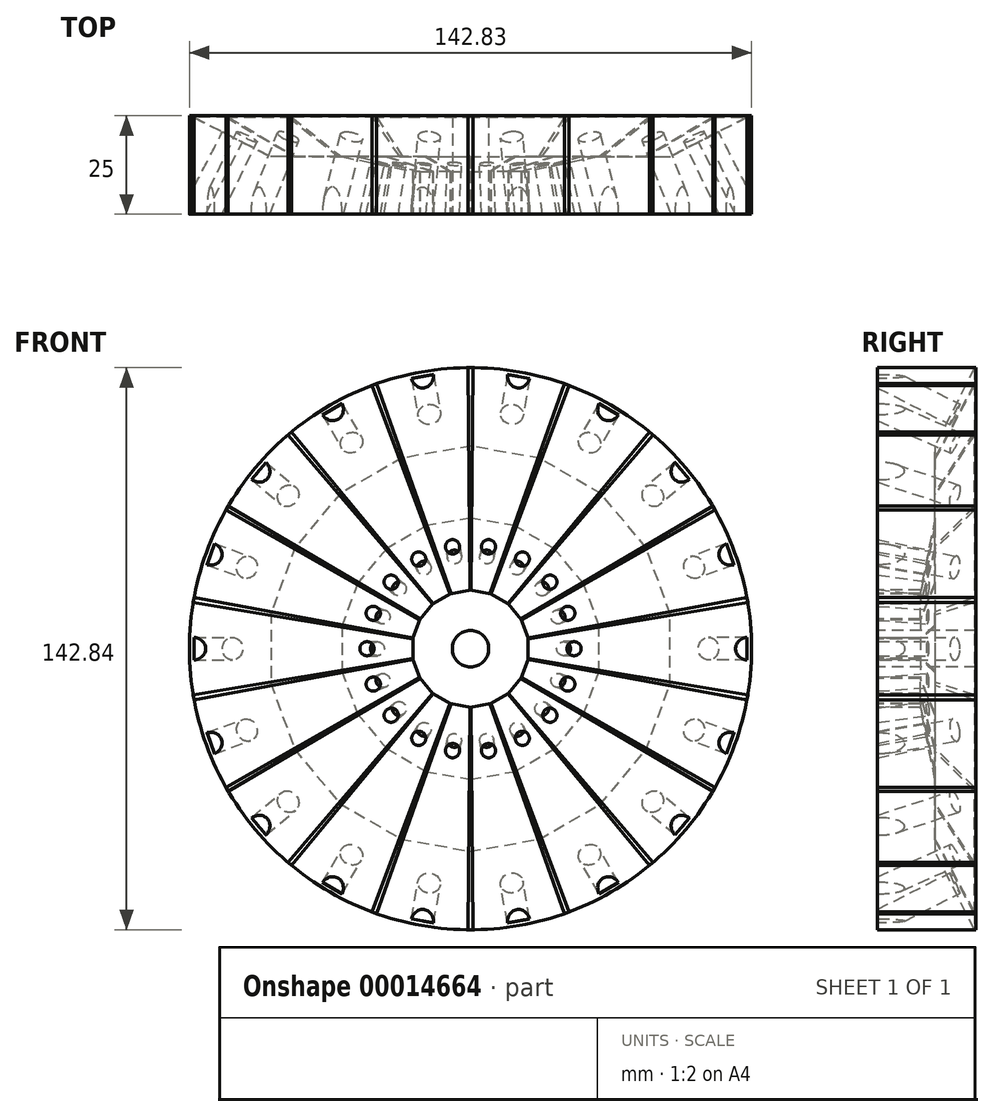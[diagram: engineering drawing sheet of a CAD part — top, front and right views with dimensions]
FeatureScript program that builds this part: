
annotation { "Feature Type Name" : "Feature", "Feature Type Description" : "" }
export const myFeature = defineFeature(function(context is Context, id is Id, definition is map)
    precondition{}
    {
        {
            var Q0;
            Q0=qCreatedBy(makeId("Top.planeOp"),FACE);
            var sketch = newSketch(context, id + "F0", { "sketchPlane" : qUnion([Q0])});
            skLineSegment(sketch, "E0.bottom", {"start": v(0, 0) * mm, "end": v(-36.04, 0) * mm});
            skLineSegment(sketch, "E0.top", {"start": v(-18.02, 14.6) * mm, "end": v(-36.04, 14.6) * mm});
            skLineSegment(sketch, "E0.left", {"start": v(0, 0) * mm, "end": v(0, 10.86) * mm});
            skLineSegment(sketch, "E0.right", {"start": v(-36.04, 0) * mm, "end": v(-36.04, 14.6) * mm});
            skLineSegment(sketch, "E1.bottom", {"start": v(-36.04, 0) * mm, "end": v(-55.59, 0) * mm});
            skLineSegment(sketch, "E1.right", {"start": v(-55.59, 0) * mm, "end": v(-55.59, 24.64) * mm});
            skLineSegment(sketch, "E2", {"start": v(-55.59, 24.64) * mm, "end": v(-36.04, 14.6) * mm});
            skLineSegment(sketch, "E3", {"start": v(-18.02, 14.6) * mm, "end": v(-18.02, 0) * mm});
            skLineSegment(sketch, "E4", {"start": v(-18.02, 14.6) * mm, "end": v(0, 10.86) * mm});
            skPoint(sketch, "E5.orphan", {"position": v(0, 14.6) * mm});
            skSolve(sketch);
        }
        {
            var Q0;
            {var subQ1=sQuery(id+"F0.wireOp",EDGE,"E0.left");Q0=makeQuery(id+"F0.imprint","IMPRINT",FACE,{"disambiguationData":[TD([[makeQuery(id+"F0.imprint","IMPRINT",EDGE,{"derivedFrom":subQ1}),1.0]])]});}
            var Q1;
            Q1=makeQuery(id+"F0.imprint","IMPRINT",FACE,{"disambiguationData":[TD([[makeQuery(id+"F0.imprint","IMPRINT",EDGE,{"derivedFrom":sQuery(id+"F0.wireOp",EDGE,"E0.top")}),1.0]])]});
            var Q2;
            Q2=makeQuery(id+"F0.imprint","IMPRINT",FACE,{"disambiguationData":[TD([[makeQuery(id+"F0.imprint","IMPRINT",EDGE,{"derivedFrom":sQuery(id+"F0.wireOp",EDGE,"E0.right")}),1.0]])]});
            extrude(context, id + "F1", {"entities" : qUnion([Q0, Q1, Q2]), "depth" : 23 * mm, "hasSecondDirection" : true, "secondDirectionOppositeDirection" : true, "secondDirectionDepth" : 3 * mm});
        }
        {
            var Q0;
            Q0=makeQuery(id+"F1.opExtrude","SWEPT_FACE",FACE,{"disambiguationData":[OSD([sQuery(id+"F0.wireOp",EDGE,"E2")])]});
            var sketch = newSketch(context, id + "F2", { "sketchPlane" : qUnion([Q0])});
            skLineSegment(sketch, "E6", {"start": v(49.72, -3) * mm, "end": v(49.72, 23) * mm, "construction": true});
            skLineSegment(sketch, "E7", {"start": v(49.72, 23) * mm, "end": v(60.7, 10) * mm, "construction": true});
            skLineSegment(sketch, "E8", {"start": v(60.7, 10) * mm, "end": v(49.72, 10) * mm, "construction": true});
            skCircle(sketch, "E9", {"center": v(49.72, 10) * mm, "radius": 4.6 * mm});
            skCircle(sketch, "E10", {"center": v(49.72, 10) * mm, "radius": 2.87 * mm});
            skSolve(sketch);
        }
        {
            var Q0;
            Q0=makeQuery(id+"F1.opExtrude","SWEPT_FACE",FACE,{"disambiguationData":[OSD([sQuery(id+"F0.wireOp",EDGE,"E4")])]});
            var sketch = newSketch(context, id + "F3", { "sketchPlane" : qUnion([Q0])});
            skCircle(sketch, "E11", {"center": v(11.41, 10) * mm, "radius": 5.8 * mm});
            skCircle(sketch, "E12", {"center": v(11.41, 10) * mm, "radius": 1.79 * mm});
            skSolve(sketch);
        }
        {
            var Q0;
            Q0=makeQuery(id+"F2.imprint","IMPRINT",FACE,{"disambiguationData":[TD([[makeQuery(id+"F2.imprint","IMPRINT",EDGE,{"derivedFrom":sQuery(id+"F2.wireOp",EDGE,"E10")}),1.0]])]});
            extrude(context, id + "F4", {"entities" : qUnion([Q0]), "operationType" : NewBodyOperationType.REMOVE, "endBound" : BoundingType.THROUGH_ALL, "oppositeDirection" : true, "depth" : 25 * mm});
        }
        {
            var Q0;
            Q0=makeQuery(id+"F3.imprint","IMPRINT",FACE,{"disambiguationData":[TD([[makeQuery(id+"F3.imprint","IMPRINT",EDGE,{"derivedFrom":sQuery(id+"F3.wireOp",EDGE,"E12")}),1.0]])]});
            extrude(context, id + "F5", {"entities" : qUnion([Q0]), "operationType" : NewBodyOperationType.REMOVE, "endBound" : BoundingType.THROUGH_ALL, "oppositeDirection" : true, "depth" : 25 * mm});
        }
        {
            var Q0;
            Q0=makeQuery(id+"F1.opExtrude","SWEPT_FACE",FACE,{"disambiguationData":[OSD([sQuery(id+"F0.wireOp",EDGE,"E0.bottom"),sQuery(id+"F0.wireOp",EDGE,"E1.bottom")])]});
            var sketch = newSketch(context, id + "F6", { "sketchPlane" : qUnion([Q0])});
            skLineSegment(sketch, "E13", {"start": v(-55.9, 10) * mm, "end": v(0, 10) * mm, "construction": true});
            skPoint(sketch, "E14.second.point", {"position": v(7.14, 10) * mm});
            skPoint(sketch, "E14.third.point", {"position": v(4.7, 13.3) * mm});
            skLineSegment(sketch, "E15", {"start": v(0, 10) * mm, "end": v(14.78, 10) * mm, "construction": true});
            skPoint(sketch, "E16.third.point", {"position": v(3.86, 13.42) * mm});
            skCircle(sketch, "E17", {"center": v(14.64, 10) * mm, "radius": 4.63 * mm});
            skSolve(sketch);
        }
        {
            var Q0;
            Q0=makeQuery(id+"F6.imprint","IMPRINT",FACE,{"disambiguationData":[TD([[makeQuery(id+"F6.imprint","IMPRINT",EDGE,{"derivedFrom":sQuery(id+"F6.wireOp",EDGE,"E17")}),1.0]])]});
            extrude(context, id + "F7", {"entities" : qUnion([Q0]), "oppositeDirection" : true, "depth" : 25 * mm});
        }
        {
            var Q0;
            Q0=qCreatedBy(makeId("Front.planeOp"),FACE);
            var sketch = newSketch(context, id + "F8", { "sketchPlane" : qUnion([Q0])});
            skCircle(sketch, "E18.0.0", {"center": v(14.64, 10) * mm, "radius": 4.63 * mm});
            skLineSegment(sketch, "E19.0.0", {"start": v(0, -3) * mm, "end": v(-18.02, -3) * mm});
            skLineSegment(sketch, "E19.0.1", {"start": v(-18.02, -3) * mm, "end": v(-18.02, 23) * mm});
            skLineSegment(sketch, "E19.0.2", {"start": v(-18.02, 23) * mm, "end": v(0, 23) * mm});
            skLineSegment(sketch, "E19.0.3", {"start": v(0, 23) * mm, "end": v(0, -3) * mm});
            skLineSegment(sketch, "E19.1.0", {"start": v(-18.02, -3) * mm, "end": v(-36.04, -3) * mm});
            skLineSegment(sketch, "E19.1.1", {"start": v(-36.04, -3) * mm, "end": v(-36.04, 23) * mm});
            skLineSegment(sketch, "E19.1.2", {"start": v(-36.04, 23) * mm, "end": v(-18.02, 23) * mm});
            skLineSegment(sketch, "E19.1.3", {"start": v(-18.02, 23) * mm, "end": v(-18.02, -3) * mm});
            skLineSegment(sketch, "E19.2.0", {"start": v(-36.04, -3) * mm, "end": v(-55.59, -3) * mm});
            skLineSegment(sketch, "E19.2.1", {"start": v(-55.59, -3) * mm, "end": v(-55.59, 28.54) * mm});
            skLineSegment(sketch, "E19.2.2", {"start": v(-55.59, 23) * mm, "end": v(-36.04, 23) * mm});
            skLineSegment(sketch, "E19.2.3", {"start": v(-36.04, 23) * mm, "end": v(-36.04, -3) * mm});
            skLineSegment(sketch, "E20", {"start": v(14.64, 10) * mm, "end": v(-55.59, -3) * mm});
            skLineSegment(sketch, "E21", {"start": v(14.64, 10) * mm, "end": v(-55.59, 23) * mm});
            skLineSegment(sketch, "E22", {"start": v(14.64, 10) * mm, "end": v(0, 10) * mm, "construction": true});
            skLineSegment(sketch, "E23", {"start": v(-55.59, -3) * mm, "end": v(-55.59, -17.72) * mm, "construction": true});
            skArc(sketch, "E24", {"start": v(-55.59, 23) * mm, "mid": v(-56.77, 10) * mm, "end": v(-55.59, -3) * mm});
            skSolve(sketch);
        }
        {
            var Q0;
            {var subQ3=sQuery(id+"F8.wireOp",EDGE,"E19.2.0");Q0=makeQuery(id+"F8.imprint","IMPRINT",FACE,{"disambiguationData":[TD([[makeQuery(id+"F8.imprint","IMPRINT",EDGE,{"derivedFrom":subQ3}),-1.0]])]});}
            var Q1;
            {var subQ3=sQuery(id+"F8.wireOp",EDGE,"E19.1.0");Q1=makeQuery(id+"F8.imprint","IMPRINT",FACE,{"disambiguationData":[TD([[makeQuery(id+"F8.imprint","IMPRINT",EDGE,{"derivedFrom":subQ3}),-1.0]])]});}
            var Q2;
            {var subQ3=sQuery(id+"F8.wireOp",EDGE,"E19.0.0");Q2=makeQuery(id+"F8.imprint","IMPRINT",FACE,{"disambiguationData":[TD([[makeQuery(id+"F8.imprint","IMPRINT",EDGE,{"derivedFrom":subQ3}),-1.0]])]});}
            var Q3;
            {var subQ3=sQuery(id+"F8.wireOp",EDGE,"E19.0.2");Q3=makeQuery(id+"F8.imprint","IMPRINT",FACE,{"disambiguationData":[TD([[makeQuery(id+"F8.imprint","IMPRINT",EDGE,{"derivedFrom":subQ3}),-1.0]])]});}
            var Q4;
            {var subQ3=sQuery(id+"F8.wireOp",EDGE,"E19.1.2");Q4=makeQuery(id+"F8.imprint","IMPRINT",FACE,{"disambiguationData":[TD([[makeQuery(id+"F8.imprint","IMPRINT",EDGE,{"derivedFrom":subQ3}),-1.0]])]});}
            var Q5;
            {var subQ3=sQuery(id+"F8.wireOp",EDGE,"E19.2.2");Q5=makeQuery(id+"F8.imprint","IMPRINT",FACE,{"disambiguationData":[TD([[makeQuery(id+"F8.imprint","IMPRINT",EDGE,{"derivedFrom":subQ3}),-1.0]])]});}
            extrude(context, id + "F9", {"entities" : qUnion([Q0, Q1, Q2, Q3, Q4, Q5]), "operationType" : NewBodyOperationType.REMOVE, "oppositeDirection" : true, "depth" : 25 * mm});
        }
        {
            var Q0;
            {var subQ0=sQuery(id+"F8.wireOp",EDGE,"E24");Q0=makeQuery(id+"F8.imprint","IMPRINT",FACE,{"disambiguationData":[TD([[makeQuery(id+"F8.imprint","IMPRINT",EDGE,{"derivedFrom":subQ0}),1.0]])]});}
            extrude(context, id + "F10", {"entities" : qUnion([Q0]), "operationType" : NewBodyOperationType.ADD, "oppositeDirection" : true, "depth" : 25 * mm});
        }
        {
            var Q0;
            Q0=makeQuery(id+"F1.opExtrude","SWEPT_BODY",BODY,{"disambiguationData":[OSD([sQuery(id+"F0.wireOp",EDGE,"E0.bottom"),sQuery(id+"F0.wireOp",EDGE,"E0.top"),sQuery(id+"F0.wireOp",EDGE,"E0.left"),sQuery(id+"F0.wireOp",EDGE,"E1.bottom"),sQuery(id+"F0.wireOp",EDGE,"E1.right"),sQuery(id+"F0.wireOp",EDGE,"E2"),sQuery(id+"F0.wireOp",EDGE,"E4")])]});
            var Q1;
            Q1=makeQuery(id+"F7.opExtrude","SWEPT_FACE",FACE,{"disambiguationData":[OSD([sQuery(id+"F6.wireOp",EDGE,"E17")])]});
            circularPattern(context, id + "F11", {"operationType" : NewBodyOperationType.ADD, "entities" : qUnion([Q0]), "axis" : qUnion([Q1]), "angle" : 20 * degree, "instanceCount" : 18});
        }
    });
